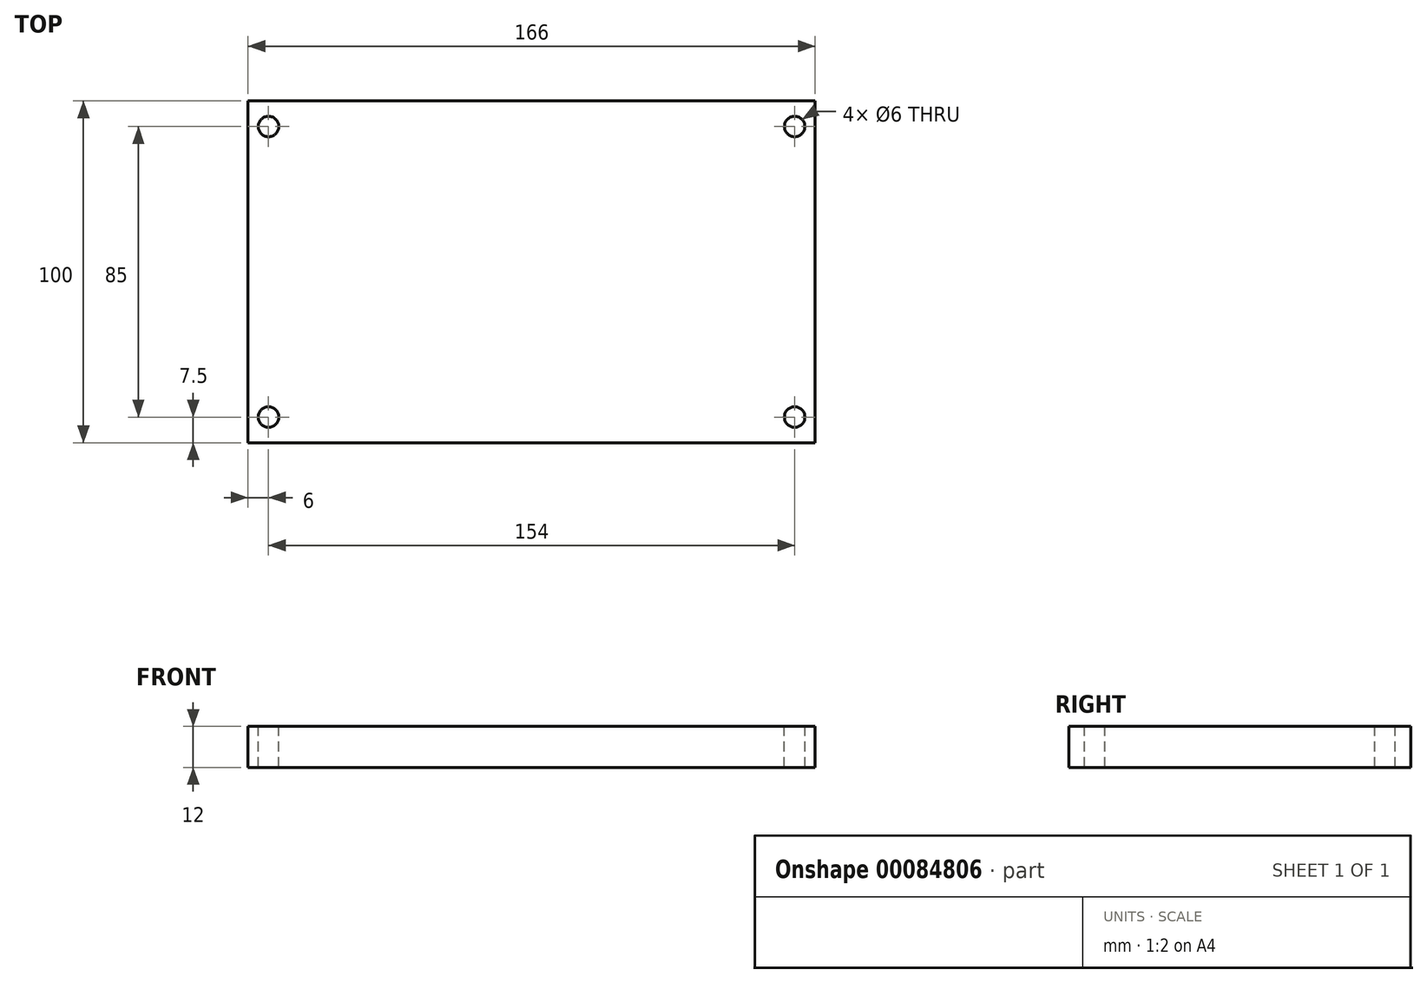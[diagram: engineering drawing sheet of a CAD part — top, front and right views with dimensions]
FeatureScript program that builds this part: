
annotation { "Feature Type Name" : "Feature", "Feature Type Description" : "" }
export const myFeature = defineFeature(function(context is Context, id is Id, definition is map)
    precondition{}
    {
        {
            var Q0;
            Q0=qCreatedBy(makeId("Top.planeOp"),FACE);
            var sketch = newSketch(context, id + "F0", { "sketchPlane" : qUnion([Q0])});
            skLineSegment(sketch, "E0.bottom", {"start": v(0, 0) * mm, "end": v(166, 0) * mm});
            skLineSegment(sketch, "E0.top", {"start": v(0, 100) * mm, "end": v(166, 100) * mm});
            skLineSegment(sketch, "E0.left", {"start": v(0, 0) * mm, "end": v(0, 100) * mm});
            skLineSegment(sketch, "E0.right", {"start": v(166, 0) * mm, "end": v(166, 100) * mm});
            skSolve(sketch);
        }
        {
            var Q0;
            Q0 = qSketchRegion(id + "F0", true);
            extrude(context, id + "F1", {"entities" : qUnion([Q0]), "depth" : 12 * mm});
        }
        {
            var Q0;
            Q0=makeQuery(id+"F1.opExtrude","CAP_FACE",FACE,{"disambiguationData":[OSD([sQuery(id+"F0.wireOp",EDGE,"E0.bottom"),sQuery(id+"F0.wireOp",EDGE,"E0.top"),sQuery(id+"F0.wireOp",EDGE,"E0.left"),sQuery(id+"F0.wireOp",EDGE,"E0.right")])],"isStart":false});
            var sketch = newSketch(context, id + "F2", { "sketchPlane" : qUnion([Q0])});
            skLineSegment(sketch, "E1.bottom", {"start": v(6, 92.5) * mm, "end": v(160, 92.5) * mm, "construction": true});
            skLineSegment(sketch, "E1.top", {"start": v(6, 7.5) * mm, "end": v(160, 7.5) * mm, "construction": true});
            skLineSegment(sketch, "E1.left", {"start": v(6, 92.5) * mm, "end": v(6, 7.5) * mm, "construction": true});
            skLineSegment(sketch, "E1.right", {"start": v(160, 92.5) * mm, "end": v(160, 7.5) * mm, "construction": true});
            skLineSegment(sketch, "E2", {"start": v(0, 50) * mm, "end": v(166, 50) * mm, "construction": true});
            skLineSegment(sketch, "E3", {"start": v(83, 100) * mm, "end": v(83, 0) * mm, "construction": true});
            skLineSegment(sketch, "E4", {"start": v(83, 92.5) * mm, "end": v(83, 7.5) * mm, "construction": true});
            skLineSegment(sketch, "E5", {"start": v(6, 50) * mm, "end": v(160, 50) * mm, "construction": true});
            skCircle(sketch, "E6", {"center": v(6, 92.5) * mm, "radius": 3 * mm});
            skCircle(sketch, "E7", {"center": v(6, 7.5) * mm, "radius": 3 * mm});
            skCircle(sketch, "E8", {"center": v(160, 7.5) * mm, "radius": 3 * mm});
            skCircle(sketch, "E9", {"center": v(160, 92.5) * mm, "radius": 3 * mm});
            skSolve(sketch);
        }
        {
            var Q0;
            Q0 = qSketchRegion(id + "F2", true);
            extrude(context, id + "F3", {"entities" : qUnion([Q0]), "operationType" : NewBodyOperationType.REMOVE, "endBound" : BoundingType.THROUGH_ALL, "oppositeDirection" : true, "depth" : 25 * mm});
        }
    });
